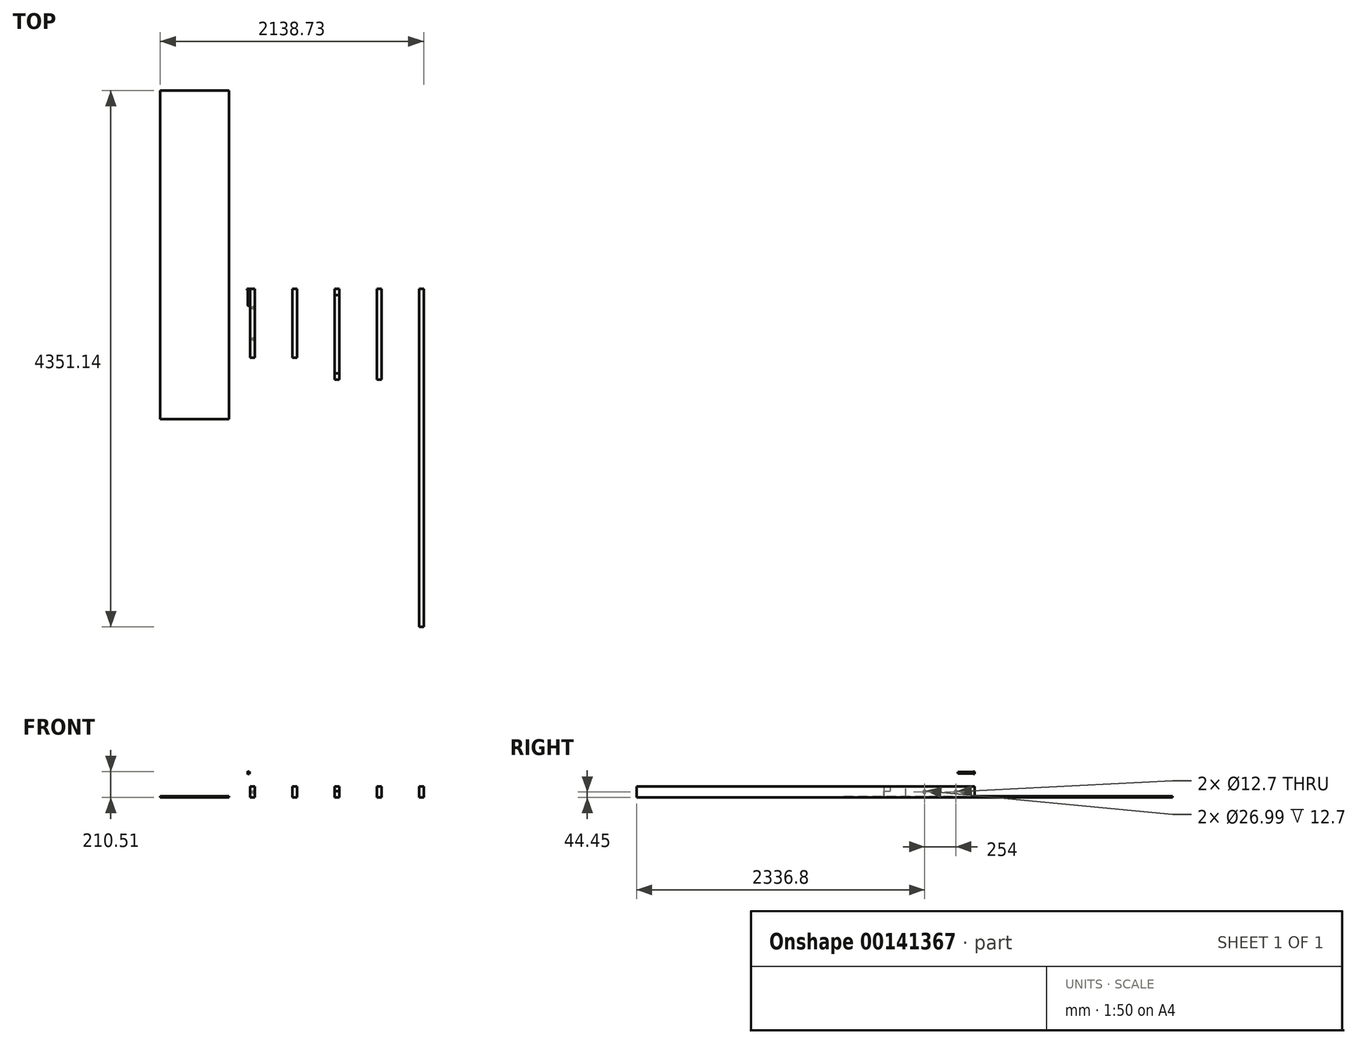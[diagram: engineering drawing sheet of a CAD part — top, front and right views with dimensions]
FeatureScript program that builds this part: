
annotation { "Feature Type Name" : "Feature", "Feature Type Description" : "" }
export const myFeature = defineFeature(function(context is Context, id is Id, definition is map)
    precondition{}
    {
        {
            var Q0;
            Q0=qCreatedBy(makeId("Front.planeOp"),FACE);
            var sketch = newSketch(context, id + "F0", { "sketchPlane" : qUnion([Q0])});
            skLineSegment(sketch, "E0.bottom", {"start": v(-1371.6, 88.9) * mm, "end": v(-1333.5, 88.9) * mm});
            skLineSegment(sketch, "E0.top", {"start": v(-1371.6, 0) * mm, "end": v(-1333.5, 0) * mm});
            skLineSegment(sketch, "E0.left", {"start": v(-1371.6, 88.9) * mm, "end": v(-1371.6, 0) * mm});
            skLineSegment(sketch, "E0.right", {"start": v(-1333.5, 88.9) * mm, "end": v(-1333.5, 0) * mm});
            skLineSegment(sketch, "E1.bottom", {"start": v(-1028.7, 0) * mm, "end": v(-990.6, 0) * mm});
            skLineSegment(sketch, "E1.top", {"start": v(-1028.7, 88.9) * mm, "end": v(-990.6, 88.9) * mm});
            skLineSegment(sketch, "E1.left", {"start": v(-1028.7, 0) * mm, "end": v(-1028.7, 88.9) * mm});
            skLineSegment(sketch, "E1.right", {"start": v(-990.6, 0) * mm, "end": v(-990.6, 88.9) * mm});
            skLineSegment(sketch, "E2.bottom", {"start": v(-685.8, 0) * mm, "end": v(-647.7, 0) * mm});
            skLineSegment(sketch, "E2.top", {"start": v(-685.8, 88.9) * mm, "end": v(-647.7, 88.9) * mm});
            skLineSegment(sketch, "E2.left", {"start": v(-685.8, 0) * mm, "end": v(-685.8, 88.9) * mm});
            skLineSegment(sketch, "E2.right", {"start": v(-647.7, 0) * mm, "end": v(-647.7, 88.9) * mm});
            skLineSegment(sketch, "E3.bottom", {"start": v(-342.9, 88.9) * mm, "end": v(-304.8, 88.9) * mm});
            skLineSegment(sketch, "E3.top", {"start": v(-342.9, 0) * mm, "end": v(-304.8, 0) * mm});
            skLineSegment(sketch, "E3.left", {"start": v(-342.9, 88.9) * mm, "end": v(-342.9, 0) * mm});
            skLineSegment(sketch, "E3.right", {"start": v(-304.8, 88.9) * mm, "end": v(-304.8, 0) * mm});
            skLineSegment(sketch, "E4.bottom", {"start": v(0, 88.9) * mm, "end": v(38.1, 88.9) * mm});
            skLineSegment(sketch, "E4.top", {"start": v(0, 0) * mm, "end": v(38.1, 0) * mm});
            skLineSegment(sketch, "E4.left", {"start": v(0, 88.9) * mm, "end": v(0, 0) * mm});
            skLineSegment(sketch, "E4.right", {"start": v(38.1, 88.9) * mm, "end": v(38.1, 0) * mm});
            skCircle(sketch, "E5.cCircle", {"center": v(-1383.72, 200.98) * mm, "radius": 9.53 * mm, "construction": true});
            skLineSegment(sketch, "E5.0", {"start": v(-1389.24, 191.46) * mm, "end": v(-1394.72, 201) * mm});
            skLineSegment(sketch, "E5.1", {"start": v(-1394.72, 201) * mm, "end": v(-1389.2, 210.51) * mm});
            skLineSegment(sketch, "E5.2", {"start": v(-1389.2, 210.51) * mm, "end": v(-1378.2, 210.49) * mm});
            skLineSegment(sketch, "E5.3", {"start": v(-1378.2, 210.49) * mm, "end": v(-1372.72, 200.95) * mm});
            skLineSegment(sketch, "E5.4", {"start": v(-1372.72, 200.95) * mm, "end": v(-1378.24, 191.44) * mm});
            skLineSegment(sketch, "E5.5", {"start": v(-1378.24, 191.44) * mm, "end": v(-1389.24, 191.46) * mm});
            skPoint(sketch, "E5.0.midPoint", {"position": v(-1391.98, 196.23) * mm});
            skSolve(sketch);
        }
        {
            var Q0;
            Q0=makeQuery(id+"F0.imprint","IMPRINT",FACE,{"disambiguationData":[TD([[makeQuery(id+"F0.imprint","IMPRINT",EDGE,{"derivedFrom":sQuery(id+"F0.wireOp",EDGE,"E4.bottom")}),-1.0]])]});
            extrude(context, id + "F1", {"entities" : qUnion([Q0]), "depth" : 2743.2 * mm});
        }
        {
            var Q0;
            Q0=makeQuery(id+"F0.imprint","IMPRINT",FACE,{"disambiguationData":[TD([[makeQuery(id+"F0.imprint","IMPRINT",EDGE,{"derivedFrom":sQuery(id+"F0.wireOp",EDGE,"E3.bottom")}),-1.0]])]});
            extrude(context, id + "F2", {"entities" : qUnion([Q0]), "depth" : 736.6 * mm});
        }
        {
            var Q0;
            Q0=makeQuery(id+"F0.imprint","IMPRINT",FACE,{"disambiguationData":[TD([[makeQuery(id+"F0.imprint","IMPRINT",EDGE,{"derivedFrom":sQuery(id+"F0.wireOp",EDGE,"E2.bottom")}),1.0]])]});
            extrude(context, id + "F3", {"entities" : qUnion([Q0]), "depth" : 736.6 * mm});
        }
        {
            var Q0;
            Q0=makeQuery(id+"F0.imprint","IMPRINT",FACE,{"disambiguationData":[TD([[makeQuery(id+"F0.imprint","IMPRINT",EDGE,{"derivedFrom":sQuery(id+"F0.wireOp",EDGE,"E1.bottom")}),1.0]])]});
            extrude(context, id + "F4", {"entities" : qUnion([Q0]), "depth" : 558.8 * mm});
        }
        {
            var Q0;
            Q0=makeQuery(id+"F0.imprint","IMPRINT",FACE,{"disambiguationData":[TD([[makeQuery(id+"F0.imprint","IMPRINT",EDGE,{"derivedFrom":sQuery(id+"F0.wireOp",EDGE,"E0.bottom")}),-1.0]])]});
            extrude(context, id + "F5", {"entities" : qUnion([Q0]), "depth" : 558.8 * mm});
        }
        {
            var Q0;
            Q0=makeQuery(id+"F3.opExtrude","SWEPT_FACE",FACE,{"disambiguationData":[OSD([sQuery(id+"F0.wireOp",EDGE,"E2.right")])]});
            var sketch = newSketch(context, id + "F6", { "sketchPlane" : qUnion([Q0])});
            skLineSegment(sketch, "E6.bottom", {"start": v(-736.6, 88.9) * mm, "end": v(-685.8, 88.9) * mm});
            skLineSegment(sketch, "E6.top", {"start": v(-736.6, 50.8) * mm, "end": v(-685.8, 50.8) * mm});
            skLineSegment(sketch, "E6.left", {"start": v(-736.6, 88.9) * mm, "end": v(-736.6, 50.8) * mm});
            skLineSegment(sketch, "E6.right", {"start": v(-685.8, 88.9) * mm, "end": v(-685.8, 50.8) * mm});
            skLineSegment(sketch, "E7.bottom", {"start": v(0, 88.9) * mm, "end": v(-50.8, 88.9) * mm});
            skLineSegment(sketch, "E7.top", {"start": v(0, 50.8) * mm, "end": v(-50.8, 50.8) * mm});
            skLineSegment(sketch, "E7.left", {"start": v(0, 88.9) * mm, "end": v(0, 50.8) * mm});
            skLineSegment(sketch, "E7.right", {"start": v(-50.8, 88.9) * mm, "end": v(-50.8, 50.8) * mm});
            skSolve(sketch);
        }
        {
            var Q0;
            Q0 = qSketchRegion(id + "F6", true);
            var Q1;
            Q1=makeQuery(id+"F3.opExtrude","SWEPT_FACE",FACE,{"disambiguationData":[OSD([sQuery(id+"F0.wireOp",EDGE,"E2.left")])]});
            extrude(context, id + "F7", {"entities" : qUnion([Q0]), "operationType" : NewBodyOperationType.REMOVE, "endBound" : BoundingType.UP_TO_SURFACE, "oppositeDirection" : true, "endBoundEntityFace" : qUnion([Q1]), "depth" : 25.4 * mm});
        }
        {
            var Q0;
            Q0=makeQuery(id+"F5.opExtrude","SWEPT_FACE",FACE,{"disambiguationData":[OSD([sQuery(id+"F0.wireOp",EDGE,"E0.right")])]});
            var sketch = newSketch(context, id + "F8", { "sketchPlane" : qUnion([Q0])});
            skCircle(sketch, "E8", {"center": v(-152.4, 44.45) * mm, "radius": 6.35 * mm});
            skCircle(sketch, "E9", {"center": v(-406.4, 44.45) * mm, "radius": 6.35 * mm});
            skCircle(sketch, "E10", {"center": v(-152.4, 44.45) * mm, "radius": 13.5 * mm});
            skCircle(sketch, "E11", {"center": v(-406.4, 44.45) * mm, "radius": 13.5 * mm});
            skSolve(sketch);
        }
        {
            var Q0;
            Q0=makeQuery(id+"F8.imprint","IMPRINT",FACE,{"disambiguationData":[TD([[makeQuery(id+"F8.imprint","IMPRINT",EDGE,{"derivedFrom":sQuery(id+"F8.wireOp",EDGE,"E8")}),1.0]])]});
            var Q1;
            Q1=makeQuery(id+"F8.imprint","IMPRINT",FACE,{"disambiguationData":[TD([[makeQuery(id+"F8.imprint","IMPRINT",EDGE,{"derivedFrom":sQuery(id+"F8.wireOp",EDGE,"E9")}),1.0]])]});
            var Q2;
            Q2=makeQuery(id+"F5.opExtrude","SWEPT_FACE",FACE,{"disambiguationData":[OSD([sQuery(id+"F0.wireOp",EDGE,"E0.left")])]});
            extrude(context, id + "F9", {"entities" : qUnion([Q0, Q1]), "operationType" : NewBodyOperationType.REMOVE, "endBound" : BoundingType.UP_TO_SURFACE, "oppositeDirection" : true, "endBoundEntityFace" : qUnion([Q2]), "depth" : 25.4 * mm});
        }
        {
            var Q0;
            Q0=qCreatedBy(makeId("Top.planeOp"),FACE);
            var sketch = newSketch(context, id + "F10", { "sketchPlane" : qUnion([Q0])});
            skLineSegment(sketch, "E12.bottom", {"start": v(-2100.63, -1059.06) * mm, "end": v(-2100.63, 1607.94) * mm});
            skLineSegment(sketch, "E12.top", {"start": v(-1541.83, -1059.06) * mm, "end": v(-1541.83, 1607.94) * mm});
            skLineSegment(sketch, "E12.left", {"start": v(-2100.63, -1059.06) * mm, "end": v(-1541.83, -1059.06) * mm});
            skLineSegment(sketch, "E12.right", {"start": v(-2100.63, 1607.94) * mm, "end": v(-1541.83, 1607.94) * mm});
            skSolve(sketch);
        }
        {
            var Q0;
            Q0 = qSketchRegion(id + "F10", true);
            extrude(context, id + "F11", {"entities" : qUnion([Q0]), "depth" : 9.52 * mm});
        }
        {
            var Q0;
            Q0=makeQuery(id+"F0.imprint","IMPRINT",FACE,{"disambiguationData":[TD([[makeQuery(id+"F0.imprint","IMPRINT",EDGE,{"derivedFrom":sQuery(id+"F0.wireOp",EDGE,"E5.0")}),-1.0]])]});
            extrude(context, id + "F12", {"entities" : qUnion([Q0]), "depth" : 9.52 * mm});
        }
        {
            var Q0;
            Q0=makeQuery(id+"F12.opExtrude","CAP_FACE",FACE,{"disambiguationData":[OSD([sQuery(id+"F0.wireOp",EDGE,"E5.0"),sQuery(id+"F0.wireOp",EDGE,"E5.1"),sQuery(id+"F0.wireOp",EDGE,"E5.2"),sQuery(id+"F0.wireOp",EDGE,"E5.3"),sQuery(id+"F0.wireOp",EDGE,"E5.4"),sQuery(id+"F0.wireOp",EDGE,"E5.5")])],"isStart":false});
            var sketch = newSketch(context, id + "F13", { "sketchPlane" : qUnion([Q0])});
            skCircle(sketch, "E13", {"center": v(-1383.7, 200.98) * mm, "radius": 6.35 * mm});
            skSolve(sketch);
        }
        {
            var Q0;
            Q0 = qSketchRegion(id + "F13", true);
            extrude(context, id + "F14", {"entities" : qUnion([Q0]), "operationType" : NewBodyOperationType.ADD, "depth" : 127 * mm});
        }
        {
            var Q0;
            Q0=makeQuery(id+"F8.imprint","IMPRINT",FACE,{"disambiguationData":[TD([[makeQuery(id+"F8.imprint","IMPRINT",EDGE,{"derivedFrom":sQuery(id+"F8.wireOp",EDGE,"E9")}),-1.0]])]});
            var Q1;
            Q1=makeQuery(id+"F8.imprint","IMPRINT",FACE,{"disambiguationData":[TD([[makeQuery(id+"F8.imprint","IMPRINT",EDGE,{"derivedFrom":sQuery(id+"F8.wireOp",EDGE,"E8")}),-1.0]])]});
            extrude(context, id + "F15", {"entities" : qUnion([Q0, Q1]), "operationType" : NewBodyOperationType.REMOVE, "oppositeDirection" : true, "depth" : 12.7 * mm});
        }
    });
